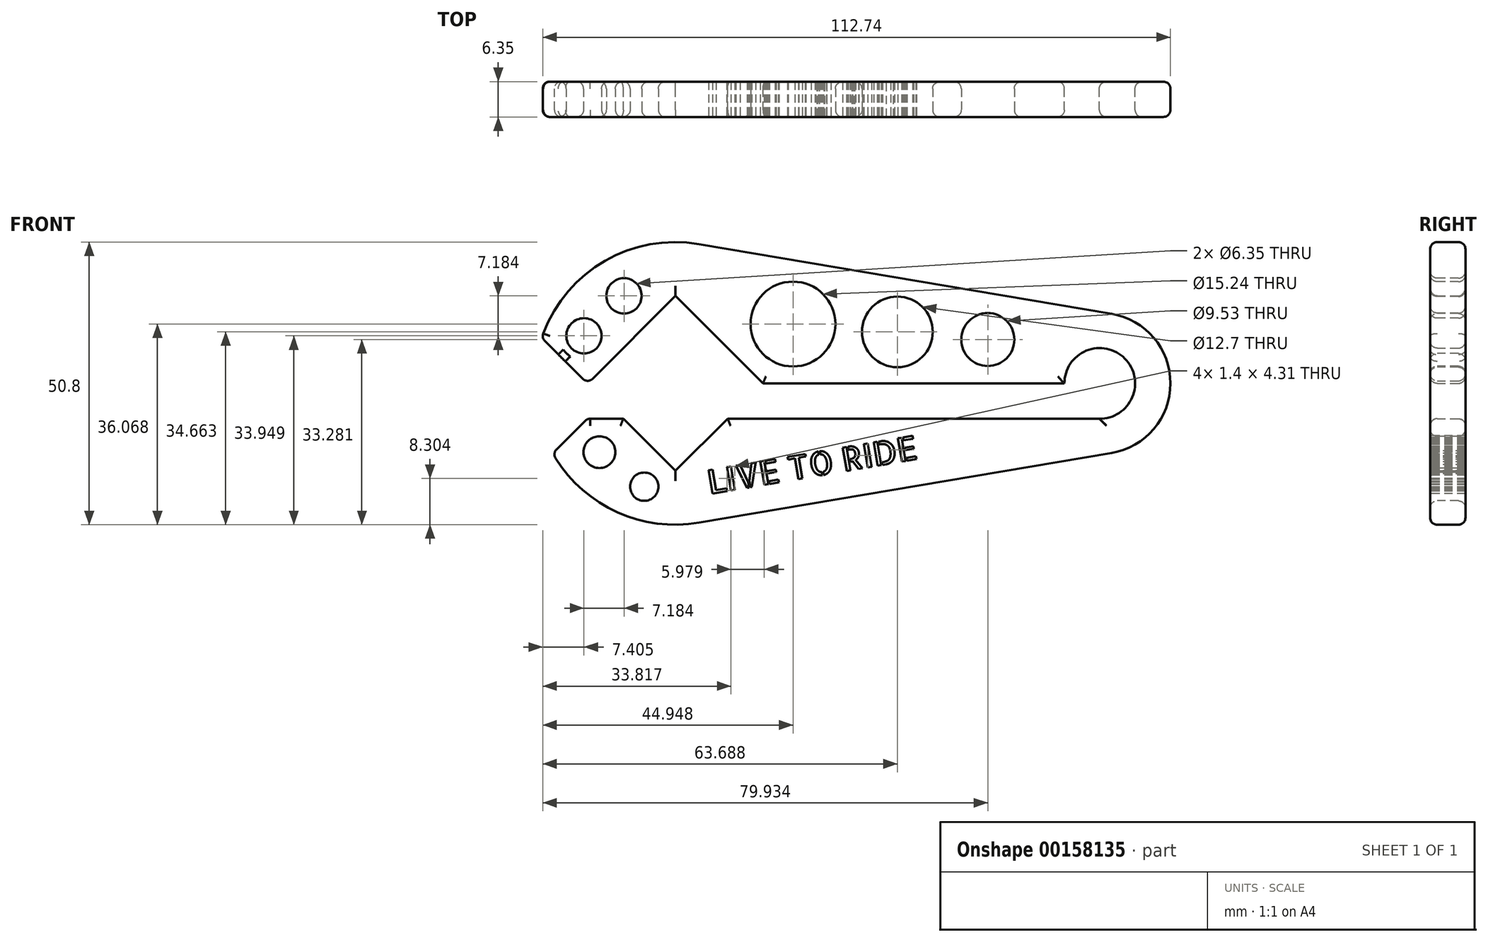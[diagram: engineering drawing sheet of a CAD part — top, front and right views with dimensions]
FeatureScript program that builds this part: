
annotation { "Feature Type Name" : "Feature", "Feature Type Description" : "" }
export const myFeature = defineFeature(function(context is Context, id is Id, definition is map)
    precondition{}
    {
        {
            var Q0;
            Q0=qCreatedBy(makeId("Front.planeOp"),FACE);
            var sketch = newSketch(context, id + "F0", { "sketchPlane" : qUnion([Q0])});
            skLineSegment(sketch, "E0.bottom", {"start": v(-36.86, 15.72) * mm, "end": v(-21.14, 0) * mm});
            skLineSegment(sketch, "E0.top", {"start": v(-46.22, -6.35) * mm, "end": v(-36.86, -15.72) * mm});
            skLineSegment(sketch, "E0.left", {"start": v(-36.86, 15.72) * mm, "end": v(-52.57, 0) * mm});
            skLineSegment(sketch, "E0.right", {"start": v(-27.5, -6.35) * mm, "end": v(-36.86, -15.72) * mm});
            skArc(sketch, "E1", {"start": v(-32.63, 25.04) * mm, "mid": v(-62.26, 0) * mm, "end": v(-32.63, -25.04) * mm});
            skArc(sketch, "E2", {"start": v(41.46, -12.52) * mm, "mid": v(52.04, 0) * mm, "end": v(41.46, 12.52) * mm});
            skLineSegment(sketch, "E3", {"start": v(-32.63, 25.04) * mm, "end": v(41.46, 12.52) * mm});
            skLineSegment(sketch, "E4", {"start": v(-32.63, -25.04) * mm, "end": v(41.46, -12.52) * mm});
            skArc(sketch, "E5", {"start": v(39.27, -6.35) * mm, "mid": v(43.86, 4.47) * mm, "end": v(33, 0) * mm});
            skLineSegment(sketch, "E6.bottom", {"start": v(39.27, -6.35) * mm, "end": v(-27.5, -6.35) * mm});
            skLineSegment(sketch, "E6.top", {"start": v(33, 0) * mm, "end": v(-75.6, 0) * mm});
            skLineSegment(sketch, "E6.left", {"start": v(39.27, -6.35) * mm, "end": v(39.27, -6.35) * mm});
            skLineSegment(sketch, "E6.right", {"start": v(-75.6, -6.35) * mm, "end": v(-75.6, 0) * mm});
            skLineSegment(sketch, "E7.trimOffspring", {"start": v(-46.22, -6.35) * mm, "end": v(-75.6, -6.35) * mm});
            skSolve(sketch);
        }
        {
            var Q0;
            {var subQ0=sQuery(id+"F0.wireOp",EDGE,"E0.bottom");Q0=makeQuery(id+"F0.imprint","IMPRINT",FACE,{"disambiguationData":[TD([[makeQuery(id+"F0.imprint","IMPRINT",EDGE,{"derivedFrom":subQ0}),1.0]])]});}
            extrude(context, id + "F1", {"entities" : qUnion([Q0]), "depth" : 6.35 * mm});
        }
        {
            var Q0;
            Q0=qCreatedBy(makeId("Front.planeOp"),FACE);
            var sketch = newSketch(context, id + "F2", { "sketchPlane" : qUnion([Q0])});
            skCircle(sketch, "E8", {"center": v(-15.75, 10.67) * mm, "radius": 7.62 * mm});
            skCircle(sketch, "E9", {"center": v(-53.3, 8.55) * mm, "radius": 3.18 * mm});
            skCircle(sketch, "E10", {"center": v(2.99, 9.26) * mm, "radius": 6.35 * mm});
            skCircle(sketch, "E11", {"center": v(-46.11, 15.73) * mm, "radius": 3.18 * mm});
            skCircle(sketch, "E12", {"center": v(19.23, 7.88) * mm, "radius": 4.76 * mm});
            skCircle(sketch, "E13", {"center": v(-50.52, -12.36) * mm, "radius": 2.86 * mm});
            skCircle(sketch, "E14", {"center": v(-42.48, -18.57) * mm, "radius": 2.54 * mm});
            skSolve(sketch);
        }
        {
            var Q0;
            Q0 = qSketchRegion(id + "F2", true);
            extrude(context, id + "F3", {"entities" : qUnion([Q0]), "operationType" : NewBodyOperationType.REMOVE, "endBound" : BoundingType.SYMMETRIC, "oppositeDirection" : true, "depth" : 25.4 * mm});
        }
        {
            var Q0;
            Q0=makeQuery(id+"F1.opExtrude","CAP_FACE",FACE,{"disambiguationData":[OSD([sQuery(id+"F0.wireOp",EDGE,"E0.bottom"),sQuery(id+"F0.wireOp",EDGE,"E0.top"),sQuery(id+"F0.wireOp",EDGE,"E0.left"),sQuery(id+"F0.wireOp",EDGE,"E0.right"),sQuery(id+"F0.wireOp",EDGE,"E1"),sQuery(id+"F0.wireOp",EDGE,"E2"),sQuery(id+"F0.wireOp",EDGE,"E3"),sQuery(id+"F0.wireOp",EDGE,"E4"),sQuery(id+"F0.wireOp",EDGE,"E5"),sQuery(id+"F0.wireOp",EDGE,"E6.bottom"),sQuery(id+"F0.wireOp",EDGE,"E6.top"),sQuery(id+"F0.wireOp",EDGE,"E6.left"),sQuery(id+"F0.wireOp",EDGE,"E7.trimOffspring")])],"isStart":false});
            var Q1;
            Q1=makeQuery(id+"F1.opExtrude","CAP_FACE",FACE,{"disambiguationData":[OSD([sQuery(id+"F0.wireOp",EDGE,"E0.bottom"),sQuery(id+"F0.wireOp",EDGE,"E0.top"),sQuery(id+"F0.wireOp",EDGE,"E0.left"),sQuery(id+"F0.wireOp",EDGE,"E0.right"),sQuery(id+"F0.wireOp",EDGE,"E1"),sQuery(id+"F0.wireOp",EDGE,"E2"),sQuery(id+"F0.wireOp",EDGE,"E3"),sQuery(id+"F0.wireOp",EDGE,"E4"),sQuery(id+"F0.wireOp",EDGE,"E5"),sQuery(id+"F0.wireOp",EDGE,"E6.bottom"),sQuery(id+"F0.wireOp",EDGE,"E6.top"),sQuery(id+"F0.wireOp",EDGE,"E6.left"),sQuery(id+"F0.wireOp",EDGE,"E7.trimOffspring")])],"isStart":true});
            fillet(context, id + "F4", {"entities" : qUnion([Q0, Q1]), "radius" : 1.27 * mm, "tangentPropagation" : true, "allowEdgeOverflow" : false});
        }
        {
            var Q0;
            Q0=makeQuery(id+"F1.opExtrude","CAP_FACE",FACE,{"disambiguationData":[OSD([sQuery(id+"F0.wireOp",EDGE,"E0.bottom"),sQuery(id+"F0.wireOp",EDGE,"E0.top"),sQuery(id+"F0.wireOp",EDGE,"E0.left"),sQuery(id+"F0.wireOp",EDGE,"E0.right"),sQuery(id+"F0.wireOp",EDGE,"E1"),sQuery(id+"F0.wireOp",EDGE,"E2"),sQuery(id+"F0.wireOp",EDGE,"E3"),sQuery(id+"F0.wireOp",EDGE,"E4"),sQuery(id+"F0.wireOp",EDGE,"E5"),sQuery(id+"F0.wireOp",EDGE,"E6.bottom"),sQuery(id+"F0.wireOp",EDGE,"E6.top"),sQuery(id+"F0.wireOp",EDGE,"E6.left"),sQuery(id+"F0.wireOp",EDGE,"E7.trimOffspring")])],"isStart":false});
            var sketch = newSketch(context, id + "F5", { "sketchPlane" : qUnion([Q0])});
            skText(sketch, "E15", { "text": "LIVE TO RIDE", "fontName": "AllertaStencil-Regular.ttf"});
            const initialGuessF5  = {"E15": [-0.03073, -0.0199, 0.98601, 0.16667, 0.00425]};
            skSetInitialGuess(sketch, initialGuessF5);
            skSolve(sketch);
        }
        {
            var Q0;
            Q0 = qSketchRegion(id + "F5", true);
            extrude(context, id + "F6", {"entities" : qUnion([Q0]), "operationType" : NewBodyOperationType.REMOVE, "endBound" : BoundingType.SYMMETRIC, "oppositeDirection" : true, "depth" : 25.4 * mm});
        }
        {
            var Q0;
            Q0=qCreatedBy(makeId("Front.planeOp"),FACE);
            var sketch = newSketch(context, id + "F7", { "sketchPlane" : qUnion([Q0])});
            skLineSegment(sketch, "E16.bottom", {"start": v(-61.6, 8.89) * mm, "end": v(-49.53, -3.17) * mm});
            skLineSegment(sketch, "E16.top", {"start": v(-73.65, -3.17) * mm, "end": v(-61.6, -15.24) * mm});
            skLineSegment(sketch, "E16.left", {"start": v(-61.6, 8.89) * mm, "end": v(-73.65, -3.17) * mm});
            skLineSegment(sketch, "E16.right", {"start": v(-49.53, -3.18) * mm, "end": v(-61.6, -15.24) * mm});
            skSolve(sketch);
        }
        {
            var Q0;
            Q0=makeQuery(id+"F7.imprint","IMPRINT",FACE,{"disambiguationData":[TD([[makeQuery(id+"F7.imprint","IMPRINT",EDGE,{"derivedFrom":sQuery(id+"F7.wireOp",EDGE,"E16.bottom")}),-1.0]])]});
            extrude(context, id + "F8", {"entities" : qUnion([Q0]), "operationType" : NewBodyOperationType.REMOVE, "endBound" : BoundingType.SYMMETRIC, "depth" : 25.4 * mm});
        }
        {
            var Q0;
            Q0=makeQuery(id+"F8.boolean.opBoolean","COPY",FACE,{"derivedFrom":makeQuery(id+"F8.opExtrude","SWEPT_FACE",FACE,{"disambiguationData":[OSD([sQuery(id+"F7.wireOp",EDGE,"E16.right")])]})});
            var Q1;
            Q1=makeQuery(id+"F8.boolean.opBoolean","COPY",FACE,{"derivedFrom":makeQuery(id+"F8.opExtrude","SWEPT_FACE",FACE,{"disambiguationData":[OSD([sQuery(id+"F7.wireOp",EDGE,"E16.bottom")])]})});
            fillet(context, id + "F9", {"entities" : qUnion([Q0, Q1]), "radius" : 1.27 * mm, "tangentPropagation" : true, "allowEdgeOverflow" : false});
        }
    });
